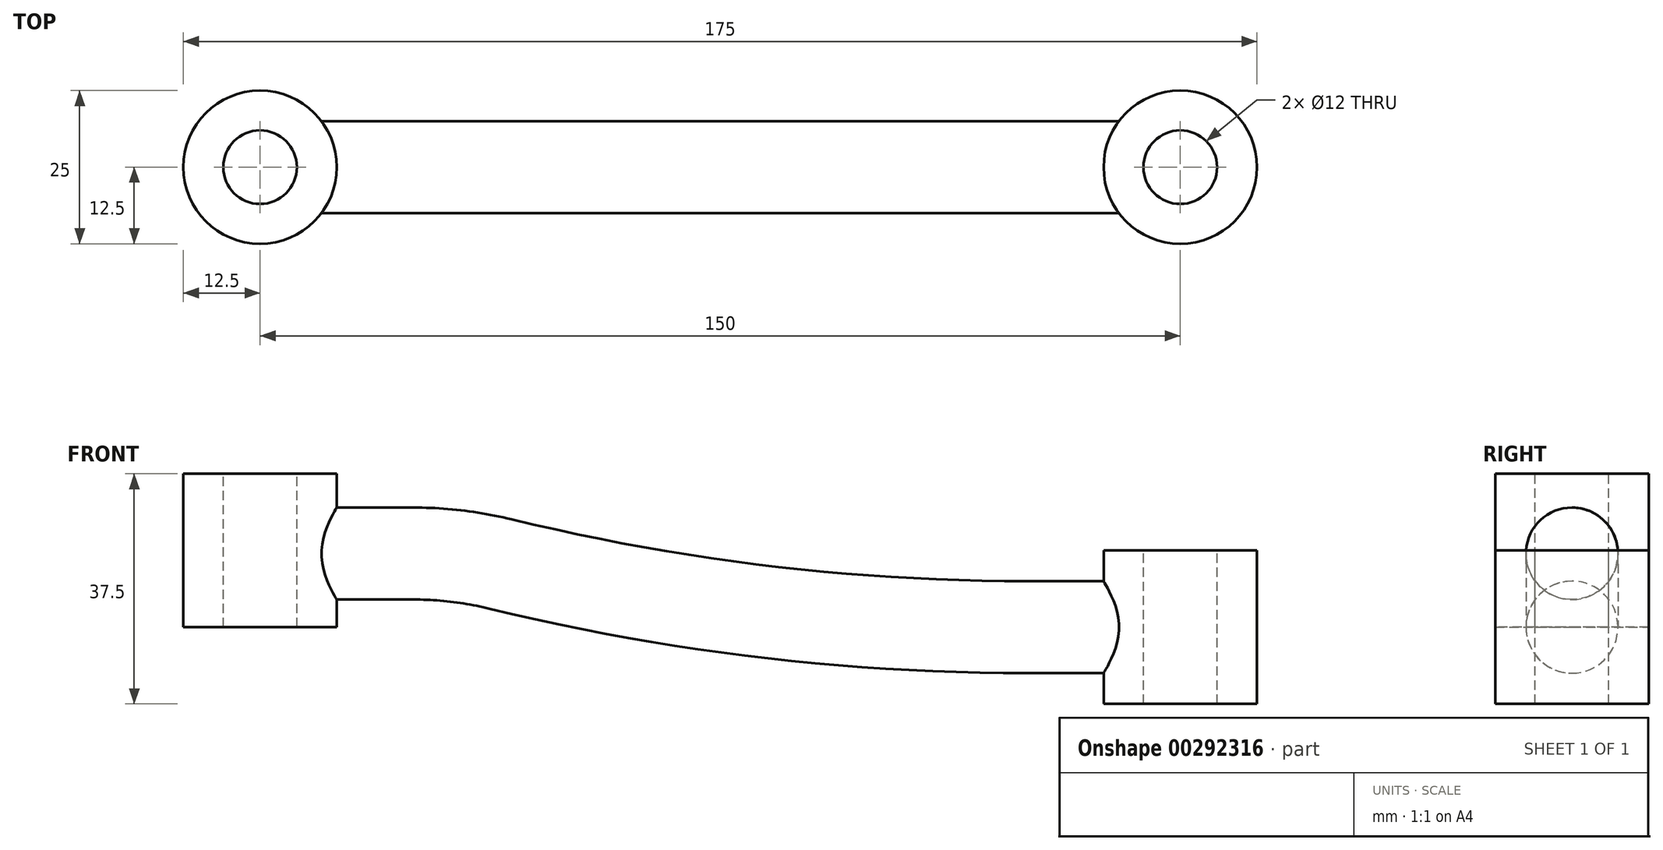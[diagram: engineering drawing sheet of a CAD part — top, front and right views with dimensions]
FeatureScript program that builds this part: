
annotation { "Feature Type Name" : "Feature", "Feature Type Description" : "" }
export const myFeature = defineFeature(function(context is Context, id is Id, definition is map)
    precondition{}
    {
        {
            var Q0;
            Q0=qCreatedBy(makeId("Top.planeOp"),FACE);
            var sketch = newSketch(context, id + "F0", { "sketchPlane" : qUnion([Q0])});
            skCircle(sketch, "E0", {"center": v(0, 0) * mm, "radius": 12.5 * mm});
            skCircle(sketch, "E1", {"center": v(150, 0) * mm, "radius": 12.5 * mm});
            skSolve(sketch);
        }
        {
            var Q0;
            Q0=makeQuery(id+"F0.imprint","IMPRINT",FACE,{"disambiguationData":[TD([[makeQuery(id+"F0.imprint","IMPRINT",EDGE,{"derivedFrom":sQuery(id+"F0.wireOp",EDGE,"E0")}),1.0]])]});
            extrude(context, id + "F1", {"entities" : qUnion([Q0]), "depth" : 25 * mm});
        }
        {
            var Q0;
            Q0=makeQuery(id+"F0.imprint","IMPRINT",FACE,{"disambiguationData":[TD([[makeQuery(id+"F0.imprint","IMPRINT",EDGE,{"derivedFrom":sQuery(id+"F0.wireOp",EDGE,"E1")}),1.0]])]});
            extrude(context, id + "F2", {"entities" : qUnion([Q0]), "endBound" : BoundingType.SYMMETRIC, "depth" : 25 * mm});
        }
        {
            var Q0;
            Q0=qCreatedBy(makeId("Front.planeOp"),FACE);
            var sketch = newSketch(context, id + "F3", { "sketchPlane" : qUnion([Q0])});
            skLineSegment(sketch, "E2", {"start": v(0, 12) * mm, "end": v(25, 12) * mm});
            skArc(sketch, "E3", {"start": v(25, 12) * mm, "mid": v(32.15, 11.57) * mm, "end": v(39.2, 10.3) * mm});
            skArc(sketch, "E4", {"start": v(39.2, 10.3) * mm, "mid": v(81.79, 2.58) * mm, "end": v(125, 0) * mm});
            skLineSegment(sketch, "E5", {"start": v(125, 0) * mm, "end": v(150, 0) * mm});
            skSolve(sketch);
        }
        {
            var Q0;
            Q0=qCreatedBy(makeId("Right.planeOp"),FACE);
            var sketch = newSketch(context, id + "F4", { "sketchPlane" : qUnion([Q0])});
            skCircle(sketch, "E6", {"center": v(0, 12) * mm, "radius": 7.5 * mm});
            skSolve(sketch);
        }
        {
            var Q0;
            Q0 = qSketchRegion(id + "F4", true);
            var Q1;
            Q1 = qConstructionFilter(qBodyType(qCreatedBy(id + "F3" ,EDGE), BodyType.WIRE), ConstructionObject.NO);
            sweep(context, id + "F5", {"operationType" : NewBodyOperationType.ADD, "profiles" : qUnion([Q0]), "path" : qUnion([Q1])});
        }
        {
            var Q0;
            Q0=makeQuery(id+"F1.opExtrude","CAP_FACE",FACE,{"disambiguationData":[OSD([sQuery(id+"F0.wireOp",EDGE,"E0")])],"isStart":false});
            var sketch = newSketch(context, id + "F6", { "sketchPlane" : qUnion([Q0])});
            skCircle(sketch, "E7", {"center": v(0, 0) * mm, "radius": 6 * mm});
            skCircle(sketch, "E8", {"center": v(150, 0) * mm, "radius": 6 * mm});
            skSolve(sketch);
        }
        {
            var Q0;
            Q0 = qSketchRegion(id + "F6", true);
            extrude(context, id + "F7", {"entities" : qUnion([Q0]), "operationType" : NewBodyOperationType.REMOVE, "endBound" : BoundingType.THROUGH_ALL, "oppositeDirection" : true, "depth" : 25 * mm});
        }
    });
